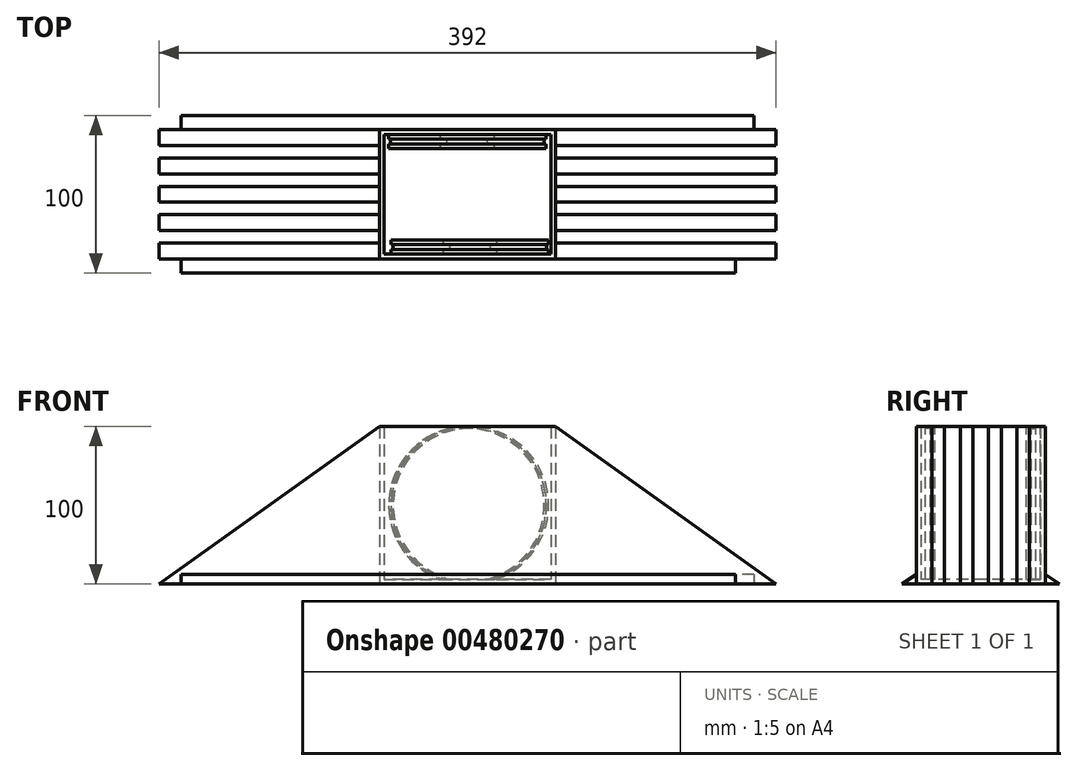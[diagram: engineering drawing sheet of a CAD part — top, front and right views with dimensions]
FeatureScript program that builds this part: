
annotation { "Feature Type Name" : "Feature", "Feature Type Description" : "" }
export const myFeature = defineFeature(function(context is Context, id is Id, definition is map)
    precondition{}
    {
        {
            var Q0;
            Q0=qCreatedBy(makeId("Top.planeOp"),FACE);
            var sketch = newSketch(context, id + "F0", { "sketchPlane" : qUnion([Q0])});
            skLineSegment(sketch, "E0", {"start": v(87, 57) * mm, "end": v(-25, 57) * mm});
            skLineSegment(sketch, "E1", {"start": v(-25, 57) * mm, "end": v(-25, -25) * mm});
            skLineSegment(sketch, "E2", {"start": v(-25, -25) * mm, "end": v(87, -25) * mm});
            skLineSegment(sketch, "E3", {"start": v(87, 57) * mm, "end": v(87, -25) * mm});
            skSolve(sketch);
        }
        {
            var Q0;
            Q0 = qSketchRegion(id + "F0", true);
            extrude(context, id + "F1", {"entities" : qUnion([Q0]), "depth" : 100 * mm});
        }
        {
            var Q0;
            Q0=makeQuery(id+"F1.opExtrude","CAP_FACE",FACE,{"disambiguationData":[OSD([sQuery(id+"F0.wireOp",EDGE,"E0"),sQuery(id+"F0.wireOp",EDGE,"E1"),sQuery(id+"F0.wireOp",EDGE,"E2"),sQuery(id+"F0.wireOp",EDGE,"E3")])],"isStart":false});
            var Q1;
            Q1=makeQuery(id+"F1.opExtrude","SWEPT_BODY",BODY,{"disambiguationData":[OSD([sQuery(id+"F0.wireOp",EDGE,"E0"),sQuery(id+"F0.wireOp",EDGE,"E1"),sQuery(id+"F0.wireOp",EDGE,"E2"),sQuery(id+"F0.wireOp",EDGE,"E3")])]});
            shell(context, id + "F2", {"entities" : qUnion([Q0]), "parts" : qUnion([Q1]), "thickness" : 3 * mm});
        }
        {
            var Q0;
            Q0=makeQuery(id+"F1.opExtrude","SWEPT_FACE",FACE,{"disambiguationData":[OSD([sQuery(id+"F0.wireOp",EDGE,"E3")])]});
            var sketch = newSketch(context, id + "F3", { "sketchPlane" : qUnion([Q0])});
            skLineSegment(sketch, "E4", {"start": v(-25, 0) * mm, "end": v(-25, 100) * mm});
            skLineSegment(sketch, "E5", {"start": v(-25, 100) * mm, "end": v(-15, 100) * mm});
            skLineSegment(sketch, "E6", {"start": v(57, 100) * mm, "end": v(47, 100) * mm});
            skLineSegment(sketch, "E7", {"start": v(47, 100) * mm, "end": v(47, 0) * mm});
            skLineSegment(sketch, "E8", {"start": v(47, 0) * mm, "end": v(57, 0) * mm});
            skLineSegment(sketch, "E9", {"start": v(57, 0) * mm, "end": v(57, 100) * mm});
            skLineSegment(sketch, "E10", {"start": v(39, 100) * mm, "end": v(39, 0) * mm});
            skLineSegment(sketch, "E11", {"start": v(39, 100) * mm, "end": v(29, 100) * mm});
            skLineSegment(sketch, "E12", {"start": v(29, 100) * mm, "end": v(29, 0) * mm});
            skLineSegment(sketch, "E13", {"start": v(29, 0) * mm, "end": v(39, 0) * mm});
            skLineSegment(sketch, "E14", {"start": v(21, 100) * mm, "end": v(21, 0) * mm});
            skLineSegment(sketch, "E15", {"start": v(21, 0) * mm, "end": v(11, 0) * mm});
            skLineSegment(sketch, "E16", {"start": v(11, 0) * mm, "end": v(11, 100) * mm});
            skLineSegment(sketch, "E17", {"start": v(3, 100) * mm, "end": v(3, 0) * mm});
            skLineSegment(sketch, "E18", {"start": v(3, 0) * mm, "end": v(-7, 0) * mm});
            skLineSegment(sketch, "E19", {"start": v(-7, 0) * mm, "end": v(-7, 100) * mm});
            skLineSegment(sketch, "E20", {"start": v(-15, 100) * mm, "end": v(-15, 0) * mm});
            skLineSegment(sketch, "E21", {"start": v(-15, 0) * mm, "end": v(-25, 0) * mm});
            skLineSegment(sketch, "E22", {"start": v(-7, 100) * mm, "end": v(3, 100) * mm});
            skLineSegment(sketch, "E23", {"start": v(11, 100) * mm, "end": v(21, 100) * mm});
            skLineSegment(sketch, "E24", {"start": v(29, 100) * mm, "end": v(39, 100) * mm});
            skSolve(sketch);
        }
        {
            var Q0;
            Q0 = qSketchRegion(id + "F3", true);
            extrude(context, id + "F4", {"entities" : qUnion([Q0]), "operationType" : NewBodyOperationType.ADD, "depth" : 140 * mm});
        }
        {
            var Q0;
            Q0=makeQuery(id+"F4.boolean.opBoolean","MERGE",FACE,{"derivedFrom":[makeQuery(id+"F1.opExtrude","SWEPT_FACE",FACE,{"disambiguationData":[OSD([sQuery(id+"F0.wireOp",EDGE,"E2")])]}),makeQuery(id+"F4.opExtrude","SWEPT_FACE",FACE,{"disambiguationData":[OSD([sQuery(id+"F3.wireOp",EDGE,"E4")])]})]});
            var sketch = newSketch(context, id + "F5", { "sketchPlane" : qUnion([Q0])});
            skLineSegment(sketch, "E25", {"start": v(227, 100) * mm, "end": v(87, 100) * mm});
            skLineSegment(sketch, "E26", {"start": v(87, 100) * mm, "end": v(227, 0) * mm});
            skSolve(sketch);
        }
        {
            var Q0;
            Q0=makeQuery(id+"F5.imprint","IMPRINT",FACE,{"disambiguationData":[TD([[makeQuery(id+"F5.imprint","IMPRINT",EDGE,{"derivedFrom":sQuery(id+"F5.wireOp",EDGE,"E25")}),-1.0]])]});
            extrude(context, id + "F6", {"entities" : qUnion([Q0]), "operationType" : NewBodyOperationType.REMOVE, "oppositeDirection" : true, "depth" : 100 * mm});
        }
        {
            var Q0;
            Q0=makeQuery(id+"F4.boolean.opBoolean","MERGE",FACE,{"derivedFrom":[makeQuery(id+"F1.opExtrude","SWEPT_FACE",FACE,{"disambiguationData":[OSD([sQuery(id+"F0.wireOp",EDGE,"E2")])]}),makeQuery(id+"F4.opExtrude","SWEPT_FACE",FACE,{"disambiguationData":[OSD([sQuery(id+"F3.wireOp",EDGE,"E4")])]})]});
            var sketch = newSketch(context, id + "F7", { "sketchPlane" : qUnion([Q0])});
            skLineSegment(sketch, "E27", {"start": v(201.15, 6) * mm, "end": v(201.15, 0) * mm});
            skLineSegment(sketch, "E28", {"start": v(201.15, 0) * mm, "end": v(201.15, 6) * mm});
            skLineSegment(sketch, "E29", {"start": v(201.15, 6) * mm, "end": v(-25, 6) * mm});
            skLineSegment(sketch, "E30", {"start": v(-25, 6) * mm, "end": v(-25, 0) * mm});
            skLineSegment(sketch, "E31", {"start": v(-25, 0) * mm, "end": v(201.15, 0) * mm});
            skSolve(sketch);
        }
        {
            var Q0;
            Q0 = qSketchRegion(id + "F7", true);
            var Q1;
            Q1 = qSketchRegion(id + "F5", true);
            extrude(context, id + "F8", {"entities" : qUnion([Q0, Q1]), "operationType" : NewBodyOperationType.ADD, "depth" : 9 * mm});
        }
        {
            var Q0;
            Q0=makeQuery(id+"F1Qfe7BfNOi0qhd_1.boolean.opBoolean","MERGE",FACE,{"derivedFrom":[makeQuery(id+"F4.boolean.opBoolean","MERGE",FACE,{"derivedFrom":[makeQuery(id+"F1.opExtrude","SWEPT_FACE",FACE,{"disambiguationData":[OSD([sQuery(id+"F0.wireOp",EDGE,"E0")])]}),makeQuery(id+"F4.opExtrude","SWEPT_FACE",FACE,{"disambiguationData":[OSD([sQuery(id+"F3.wireOp",EDGE,"E9")])]})]}),makeQuery(id+"F1Qfe7BfNOi0qhd_1.opExtrude","SWEPT_FACE",FACE,{"disambiguationData":[OSD([sQuery(id+"F4n8gGMwtmUvW1U_1.wireOp",EDGE,"d62e5a9a-93b0-4003-a0d4-11d03c5e42fc")])]})]});
            var sketch = newSketch(context, id + "F9", { "sketchPlane" : qUnion([Q0])});
            skSolve(sketch);
        }
        {
            var Q0;
            Q0=makeQuery(id+"F2.opShell","OFFSET_FACE",FACE,{"disambiguationData":[OSD([sQuery(id+"F0.wireOp",EDGE,"E0")])]});
            var sketch = newSketch(context, id + "F10", { "sketchPlane" : qUnion([Q0])});
            skLineSegment(sketch, "E32", {"start": v(31, 100) * mm, "end": v(31, 0) * mm});
            skCircle(sketch, "E33", {"center": v(31, 50) * mm, "radius": 50 * mm});
            skSolve(sketch);
        }
        {
            var Q0;
            Q0 = qSketchRegion(id + "F10", true);
            extrude(context, id + "F11", {"entities" : qUnion([Q0]), "operationType" : NewBodyOperationType.ADD, "depth" : 3 * mm});
        }
        {
            var Q0;
            Q0=makeQuery(id+"F11.opExtrude","CAP_FACE",FACE,{"disambiguationData":[OSD([sQuery(id+"F10.wireOp",EDGE,"E33")])],"isStart":false});
            var sketch = newSketch(context, id + "F12", { "sketchPlane" : qUnion([Q0])});
            skCircle(sketch, "E34", {"center": v(31, 50) * mm, "radius": 48.73 * mm});
            skSolve(sketch);
        }
        {
            var Q0;
            Q0 = qSketchRegion(id + "F12", true);
            extrude(context, id + "F13", {"entities" : qUnion([Q0]), "operationType" : NewBodyOperationType.ADD, "depth" : 3 * mm});
        }
        {
            var Q0;
            Q0=makeQuery(id+"F13.opExtrude","CAP_FACE",FACE,{"disambiguationData":[OSD([sQuery(id+"F12.wireOp",EDGE,"E34")])],"isStart":false});
            var sketch = newSketch(context, id + "F14", { "sketchPlane" : qUnion([Q0])});
            skCircle(sketch, "E35", {"center": v(31, 50) * mm, "radius": 50 * mm});
            skSolve(sketch);
        }
        {
            var Q0;
            Q0 = qSketchRegion(id + "F14", true);
            extrude(context, id + "F15", {"entities" : qUnion([Q0]), "operationType" : NewBodyOperationType.ADD, "depth" : 3 * mm});
        }
        {
            var Q0;
            Q0=makeQuery(id+"F1.opExtrude","SWEPT_FACE",FACE,{"disambiguationData":[OSD([sQuery(id+"F0.wireOp",EDGE,"E1")])]});
            var sketch = newSketch(context, id + "F16", { "sketchPlane" : qUnion([Q0])});
            skLineSegment(sketch, "E36.0", {"start": v(-47, 100) * mm, "end": v(-47, 0) * mm});
            skLineSegment(sketch, "E36.1", {"start": v(-39, 100) * mm, "end": v(-39, 0) * mm});
            skLineSegment(sketch, "E36.2", {"start": v(-29, 100) * mm, "end": v(-29, 0) * mm});
            skLineSegment(sketch, "E36.3", {"start": v(-21, 100) * mm, "end": v(-21, 0) * mm});
            skLineSegment(sketch, "E36.4", {"start": v(-11, 0) * mm, "end": v(-11, 100) * mm});
            skLineSegment(sketch, "E36.5", {"start": v(-3, 100) * mm, "end": v(-3, 0) * mm});
            skLineSegment(sketch, "E36.6", {"start": v(7, 0) * mm, "end": v(7, 100) * mm});
            skLineSegment(sketch, "E36.7", {"start": v(15, 100) * mm, "end": v(15, 0) * mm});
            skLineSegment(sketch, "E37", {"start": v(-57, 100) * mm, "end": v(-47, 100) * mm});
            skLineSegment(sketch, "E38", {"start": v(-57, 0) * mm, "end": v(-47, 0) * mm});
            skLineSegment(sketch, "E39", {"start": v(-57, 0) * mm, "end": v(-57, 100) * mm});
            skLineSegment(sketch, "E40", {"start": v(-39, 100) * mm, "end": v(-29, 100) * mm});
            skLineSegment(sketch, "E41", {"start": v(-39, 0) * mm, "end": v(-29, 0) * mm});
            skLineSegment(sketch, "E42", {"start": v(-21, 100) * mm, "end": v(-11, 100) * mm});
            skLineSegment(sketch, "E43", {"start": v(-21, 0) * mm, "end": v(-11, 0) * mm});
            skLineSegment(sketch, "E44", {"start": v(-3, 100) * mm, "end": v(7, 100) * mm});
            skLineSegment(sketch, "E45", {"start": v(-3, 0) * mm, "end": v(7, 0) * mm});
            skLineSegment(sketch, "E46", {"start": v(15, 100) * mm, "end": v(25, 100) * mm});
            skLineSegment(sketch, "E47", {"start": v(25, 0) * mm, "end": v(15, 0) * mm});
            skLineSegment(sketch, "E48", {"start": v(25, 100) * mm, "end": v(25, 0) * mm});
            skSolve(sketch);
        }
        {
            var Q0;
            Q0 = qSketchRegion(id + "F16", true);
            extrude(context, id + "F17", {"entities" : qUnion([Q0]), "operationType" : NewBodyOperationType.ADD, "depth" : 140 * mm});
        }
        {
            var Q0;
            Q0=makeQuery(id+"F17.boolean.opBoolean","MERGE",FACE,{"derivedFrom":[makeQuery(id+"F4.boolean.opBoolean","MERGE",FACE,{"derivedFrom":[makeQuery(id+"F1.opExtrude","SWEPT_FACE",FACE,{"disambiguationData":[OSD([sQuery(id+"F0.wireOp",EDGE,"E2")])]}),makeQuery(id+"F4.opExtrude","SWEPT_FACE",FACE,{"disambiguationData":[OSD([sQuery(id+"F3.wireOp",EDGE,"E4")])]})]}),makeQuery(id+"F17.opExtrude","SWEPT_FACE",FACE,{"disambiguationData":[OSD([sQuery(id+"F16.wireOp",EDGE,"H6bkzeH7-jNOE-3UQa-XwI6-GzcXzXf3ximg")])]})]});
            var sketch = newSketch(context, id + "F18", { "sketchPlane" : qUnion([Q0])});
            skLineSegment(sketch, "E49", {"start": v(-165, 0) * mm, "end": v(-165, 100) * mm});
            skLineSegment(sketch, "E50", {"start": v(-165, 100) * mm, "end": v(-25, 100) * mm});
            skLineSegment(sketch, "E51", {"start": v(-25, 100) * mm, "end": v(-165, 0) * mm});
            skSolve(sketch);
        }
        {
            var Q0;
            Q0 = qSketchRegion(id + "F18", true);
            extrude(context, id + "F19", {"entities" : qUnion([Q0]), "operationType" : NewBodyOperationType.REMOVE, "oppositeDirection" : true, "depth" : 82 * mm});
        }
        {
            var Q0;
            Q0=makeQuery(id+"F2.opShell","OFFSET_FACE",FACE,{"disambiguationData":[OSD([sQuery(id+"F0.wireOp",EDGE,"E2")])]});
            var sketch = newSketch(context, id + "F20", { "sketchPlane" : qUnion([Q0])});
            skCircle(sketch, "E52", {"center": v(-32.5, 50) * mm, "radius": 50 * mm});
            skLineSegment(sketch, "E53", {"start": v(22, 100) * mm, "end": v(22, 0) * mm});
            skPoint(sketch, "E54.0", {"position": v(-87, 100) * mm});
            skLineSegment(sketch, "E55", {"start": v(-87, 100) * mm, "end": v(-87, 0) * mm});
            skLineSegment(sketch, "E56", {"start": v(-87, 50) * mm, "end": v(22, 50) * mm});
            skSolve(sketch);
        }
        {
            var Q0;
            Q0 = qSketchRegion(id + "F20", true);
            extrude(context, id + "F21", {"entities" : qUnion([Q0]), "operationType" : NewBodyOperationType.ADD, "depth" : 3 * mm});
        }
        {
            var Q0;
            Q0=makeQuery(id+"F21.opExtrude","CAP_FACE",FACE,{"disambiguationData":[OSD([sQuery(id+"F20.wireOp",EDGE,"E52")])],"isStart":false});
            var sketch = newSketch(context, id + "F22", { "sketchPlane" : qUnion([Q0])});
            skCircle(sketch, "E57", {"center": v(-32.5, 50) * mm, "radius": 48.73 * mm});
            skSolve(sketch);
        }
        {
            var Q0;
            Q0 = qSketchRegion(id + "F22", true);
            extrude(context, id + "F23", {"entities" : qUnion([Q0]), "operationType" : NewBodyOperationType.ADD, "depth" : 3 * mm});
        }
        {
            var Q0;
            Q0=makeQuery(id+"F23.opExtrude","CAP_FACE",FACE,{"disambiguationData":[OSD([sQuery(id+"F22.wireOp",EDGE,"E57")])],"isStart":false});
            var sketch = newSketch(context, id + "F24", { "sketchPlane" : qUnion([Q0])});
            skCircle(sketch, "E58", {"center": v(-32.5, 50) * mm, "radius": 50 * mm});
            skSolve(sketch);
        }
        {
            var Q0;
            Q0 = qSketchRegion(id + "F24", true);
            extrude(context, id + "F25", {"entities" : qUnion([Q0]), "operationType" : NewBodyOperationType.ADD, "depth" : 3 * mm});
        }
        {
            var Q0;
            {var subQ8=makeQuery(id+"F17.opExtrude","SWEPT_FACE",FACE,{"disambiguationData":[OSD([sQuery(id+"F16.wireOp",EDGE,"H6bkzeH7-jNOE-3UQa-XwI6-GzcXzXf3ximg")])]});var subQ12=sQuery(id+"F0.wireOp",EDGE,"E2");var subQ25=makeQuery(id+"F1.opExtrude","SWEPT_FACE",FACE,{"disambiguationData":[OSD([subQ12])]});var subQ28=makeQuery(id+"F4.opExtrude","SWEPT_FACE",FACE,{"disambiguationData":[OSD([sQuery(id+"F3.wireOp",EDGE,"E4")])]});Q0=makeQuery(id+"F21.boolean.opBoolean","SPLIT",FACE,{"disambiguationData":[TD([makeQuery(id+"F19.boolean.opBoolean","COPY",FACE,{"disambiguationData":[TD([subQ25])],"derivedFrom":makeQuery(id+"F19.opExtrude","SWEPT_FACE",FACE,{"disambiguationData":[OSD([sQuery(id+"F18.wireOp",EDGE,"E51")])]})})])],"derivedFrom":makeQuery(id+"F17.boolean.opBoolean","MERGE",FACE,{"derivedFrom":[makeQuery(id+"F4.boolean.opBoolean","MERGE",FACE,{"derivedFrom":[subQ25,subQ28]}),subQ8]})});}
            var sketch = newSketch(context, id + "F26", { "sketchPlane" : qUnion([Q0])});
            skLineSegment(sketch, "E59", {"start": v(-25, 100) * mm, "end": v(-25, 0) * mm});
            skLineSegment(sketch, "E60", {"start": v(-151, 6) * mm, "end": v(-151, 0) * mm});
            skLineSegment(sketch, "E61", {"start": v(-25, 6) * mm, "end": v(-25, 0) * mm});
            skLineSegment(sketch, "E62", {"start": v(-151, 6) * mm, "end": v(-25, 6) * mm});
            skLineSegment(sketch, "E63", {"start": v(-151, 0) * mm, "end": v(-25, 0) * mm});
            skSolve(sketch);
        }
        {
            var Q0;
            Q0 = qSketchRegion(id + "F26", true);
            extrude(context, id + "F27", {"entities" : qUnion([Q0]), "operationType" : NewBodyOperationType.ADD, "depth" : 9 * mm});
        }
        {
            var Q0;
            Q0=makeQuery(id+"F27.opExtrude","SWEPT_FACE",FACE,{"disambiguationData":[OSD([sQuery(id+"F26.wireOp",EDGE,"E60")])]});
            var sketch = newSketch(context, id + "F28", { "sketchPlane" : qUnion([Q0])});
            skLineSegment(sketch, "E64", {"start": v(25, 6) * mm, "end": v(34, 6) * mm});
            skLineSegment(sketch, "E65", {"start": v(34, 6) * mm, "end": v(34, 6) * mm});
            skLineSegment(sketch, "E66", {"start": v(25, 6) * mm, "end": v(34, 0) * mm});
            skLineSegment(sketch, "E67", {"start": v(34, 0) * mm, "end": v(34, 6) * mm});
            skSolve(sketch);
        }
        {
            var Q0;
            {var subQ0=sQuery(id+"F0.wireOp",EDGE,"E0");Q0=makeQuery(id+"F9.imprint","IMPRINT",FACE,{"disambiguationData":[TD([[makeQuery(id+"F9.imprint","IMPRINT",EDGE,{"derivedFrom":makeQuery(id+"F1.opExtrude","SWEPT_EDGE",EDGE,{"disambiguationData":[OSD([subQ0,sQuery(id+"F0.wireOp",EDGE,"E1")])]})}),-1.0]])]});}
            var sketch = newSketch(context, id + "F29", { "sketchPlane" : qUnion([Q0])});
            skPoint(sketch, "E68.0", {"position": v(-87, 100) * mm});
            skPoint(sketch, "E69.0", {"position": v(25, 100) * mm});
            skLineSegment(sketch, "E70", {"start": v(-213, 6) * mm, "end": v(-213, 0) * mm});
            skLineSegment(sketch, "E71", {"start": v(151, 6) * mm, "end": v(151, 0) * mm});
            skLineSegment(sketch, "E72", {"start": v(-213, 6) * mm, "end": v(151, 6) * mm});
            skLineSegment(sketch, "E73", {"start": v(151, 0) * mm, "end": v(-213, 0) * mm});
            skSolve(sketch);
        }
        {
            var Q0;
            Q0 = qSketchRegion(id + "F29", true);
            extrude(context, id + "F30", {"entities" : qUnion([Q0]), "operationType" : NewBodyOperationType.ADD, "depth" : 9 * mm});
        }
        {
            var Q0;
            Q0=makeQuery(id+"F30.opExtrude","SWEPT_FACE",FACE,{"disambiguationData":[OSD([sQuery(id+"F29.wireOp",EDGE,"E70")])]});
            var sketch = newSketch(context, id + "F31", { "sketchPlane" : qUnion([Q0])});
            skLineSegment(sketch, "E74", {"start": v(57, 6) * mm, "end": v(66, 0) * mm});
            skLineSegment(sketch, "E75", {"start": v(66, 0) * mm, "end": v(66, 6) * mm});
            skLineSegment(sketch, "E76", {"start": v(66, 6) * mm, "end": v(57, 6) * mm});
            skSolve(sketch);
        }
        {
            var Q0;
            Q0 = qSketchRegion(id + "F31", true);
            extrude(context, id + "F32", {"entities" : qUnion([Q0]), "operationType" : NewBodyOperationType.REMOVE, "oppositeDirection" : true, "depth" : 372 * mm});
        }
        {
            var Q0;
            Q0 = qSketchRegion(id + "F28", true);
            extrude(context, id + "F33", {"entities" : qUnion([Q0]), "operationType" : NewBodyOperationType.REMOVE, "oppositeDirection" : true, "depth" : 356 * mm});
        }
    });
